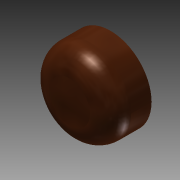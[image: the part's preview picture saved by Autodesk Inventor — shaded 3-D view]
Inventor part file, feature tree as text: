
AUTODESK INVENTOR PART (.ipt)
format: ipt  version: 2015 (Build 190159000, 159)  size: 104,448 bytes
history: native  units: in
note: dims shown in document units (in); Inventor stores cm internally (conversion verified against a paired STEP export)
features: extrude x1, fillet x1, sketch x1
ambient origin geometry x8: Origin, YZ Plane, XZ Plane, XY Plane, X Axis, Y Axis, Z Axis, Center Point
bodies: Solid1 (feature_tree)
feature tree (3):
  extrude  "Extrusion1"  Depth=0.125in TaperAngle=0.0deg
  fillet  "Fillet1"  Radius=0.0625in
  sketch  "Sketch1"  dims[d0=0.25in d1=0.125in d2=0.0in d3=0.0625in]
